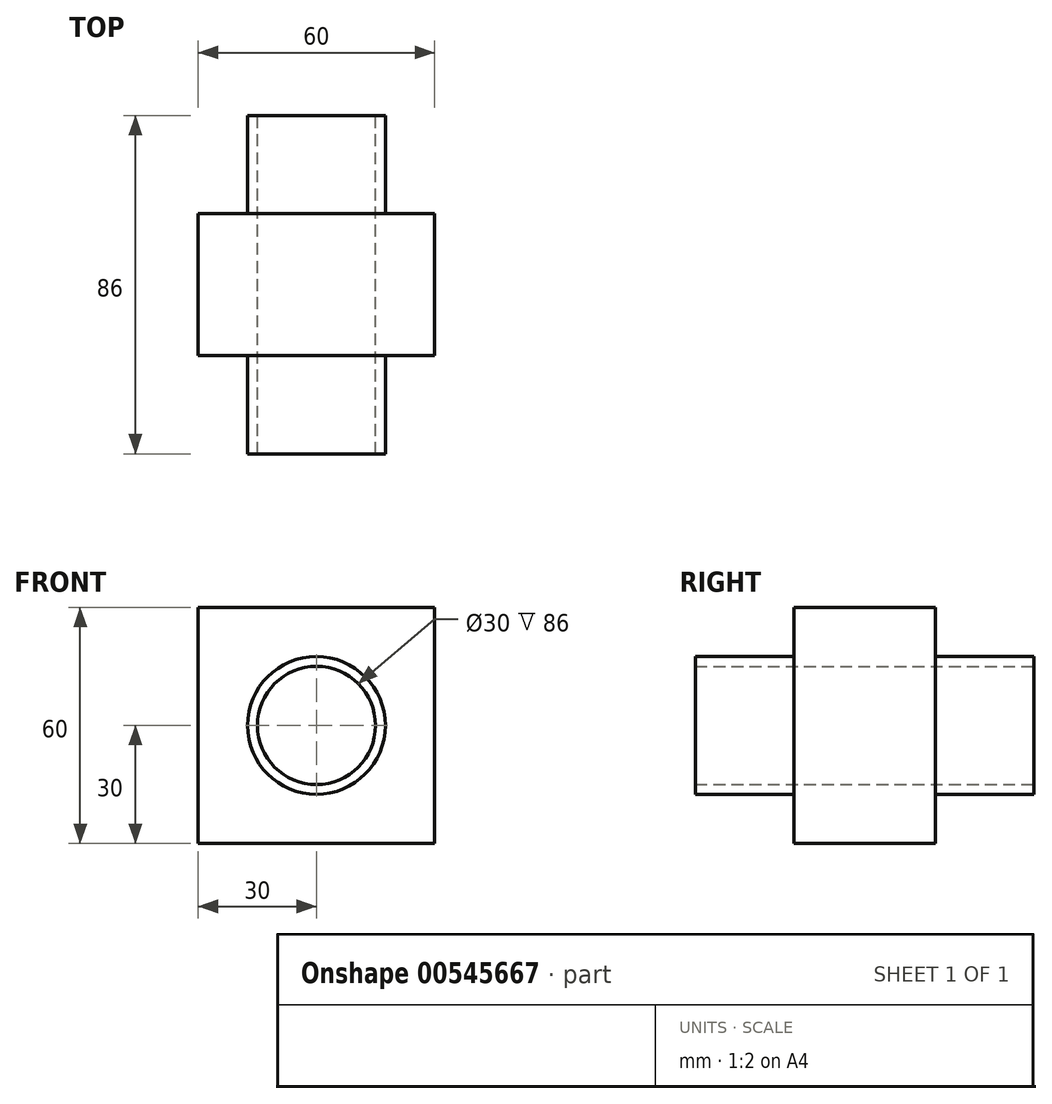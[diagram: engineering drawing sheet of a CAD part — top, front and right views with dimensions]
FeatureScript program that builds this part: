
annotation { "Feature Type Name" : "Feature", "Feature Type Description" : "" }
export const myFeature = defineFeature(function(context is Context, id is Id, definition is map)
    precondition{}
    {
        {
            var Q0;
            Q0=qCreatedBy(makeId("Front.planeOp"),FACE);
            var sketch = newSketch(context, id + "F0", { "sketchPlane" : qUnion([Q0])});
            skLineSegment(sketch, "E0.bottom", {"start": v(-30, 30) * mm, "end": v(30, 30) * mm});
            skLineSegment(sketch, "E0.top", {"start": v(-30, -30) * mm, "end": v(30, -30) * mm});
            skLineSegment(sketch, "E0.left", {"start": v(-30, 30) * mm, "end": v(-30, -30) * mm});
            skLineSegment(sketch, "E0.right", {"start": v(30, 30) * mm, "end": v(30, -30) * mm});
            skSolve(sketch);
        }
        {
            var Q0;
            Q0=makeQuery(id+"F0.imprint","IMPRINT",FACE,{"disambiguationData":[TD([[makeQuery(id+"F0.imprint","IMPRINT",EDGE,{"derivedFrom":sQuery(id+"F0.wireOp",EDGE,"E0.bottom")}),-1.0]])]});
            extrude(context, id + "F1", {"entities" : qUnion([Q0]), "oppositeDirection" : true, "depth" : 36 * mm, "offsetDistance" : 25 * mm});
        }
        {
            var Q0;
            Q0=makeQuery(id+"F1.opExtrude","CAP_FACE",FACE,{"disambiguationData":[OSD([sQuery(id+"F0.wireOp",EDGE,"E0.bottom"),sQuery(id+"F0.wireOp",EDGE,"E0.top"),sQuery(id+"F0.wireOp",EDGE,"E0.left"),sQuery(id+"F0.wireOp",EDGE,"E0.right")])],"isStart":true});
            var sketch = newSketch(context, id + "F2", { "sketchPlane" : qUnion([Q0])});
            skCircle(sketch, "E1", {"center": v(0, 0) * mm, "radius": 17.5 * mm});
            skCircle(sketch, "E2", {"center": v(0, 0) * mm, "radius": 17.77 * mm});
            skSolve(sketch);
        }
        {
            var Q0;
            Q0=makeQuery(id+"F2.imprint","IMPRINT",FACE,{"disambiguationData":[TD([[makeQuery(id+"F2.imprint","IMPRINT",EDGE,{"derivedFrom":sQuery(id+"F2.wireOp",EDGE,"E1")}),1.0]])]});
            extrude(context, id + "F3", {"entities" : qUnion([Q0]), "operationType" : NewBodyOperationType.ADD, "depth" : 25 * mm, "offsetDistance" : 25 * mm});
        }
        {
            var Q0;
            Q0=makeQuery(id+"F1.opExtrude","CAP_FACE",FACE,{"disambiguationData":[OSD([sQuery(id+"F0.wireOp",EDGE,"E0.bottom"),sQuery(id+"F0.wireOp",EDGE,"E0.top"),sQuery(id+"F0.wireOp",EDGE,"E0.left"),sQuery(id+"F0.wireOp",EDGE,"E0.right")])],"isStart":false});
            var sketch = newSketch(context, id + "F4", { "sketchPlane" : qUnion([Q0])});
            skCircle(sketch, "E3", {"center": v(0, 0) * mm, "radius": 17.5 * mm});
            skSolve(sketch);
        }
        {
            var Q0;
            Q0=makeQuery(id+"F4.imprint","IMPRINT",FACE,{"disambiguationData":[TD([[makeQuery(id+"F4.imprint","IMPRINT",EDGE,{"derivedFrom":sQuery(id+"F4.wireOp",EDGE,"E3")}),1.0]])]});
            extrude(context, id + "F5", {"entities" : qUnion([Q0]), "operationType" : NewBodyOperationType.ADD, "depth" : 25 * mm, "offsetDistance" : 25 * mm});
        }
        {
            var Q0;
            Q0=makeQuery(id+"F5.opExtrude","CAP_FACE",FACE,{"disambiguationData":[OSD([sQuery(id+"F4.wireOp",EDGE,"E3")])],"isStart":false});
            var sketch = newSketch(context, id + "F6", { "sketchPlane" : qUnion([Q0])});
            skCircle(sketch, "E4", {"center": v(0, 0) * mm, "radius": 13 * mm});
            skSolve(sketch);
        }
        {
            var Q0;
            Q0=sQuery(id+"F6.wireOp",VERTEX,"E4.center");
            var Q1;
            Q1=makeQuery(id+"F1.opExtrude","SWEPT_BODY",BODY,{"disambiguationData":[OSD([sQuery(id+"F0.wireOp",EDGE,"E0.bottom"),sQuery(id+"F0.wireOp",EDGE,"E0.top"),sQuery(id+"F0.wireOp",EDGE,"E0.left"),sQuery(id+"F0.wireOp",EDGE,"E0.right")])]});
            hole(context, id + "F7", {"style" : HoleStyle.SIMPLE, "endStyle" : HoleEndStyle.THROUGH, "holeDiameter" : 30 * mm, "majorDiameter" : 5 * mm, "isTappedThrough" : true, "tappedDepth" : 12 * mm, "tapClearance" : 3, "locations" : qUnion([Q0]), "scope" : qUnion([Q1])});
        }
    });
